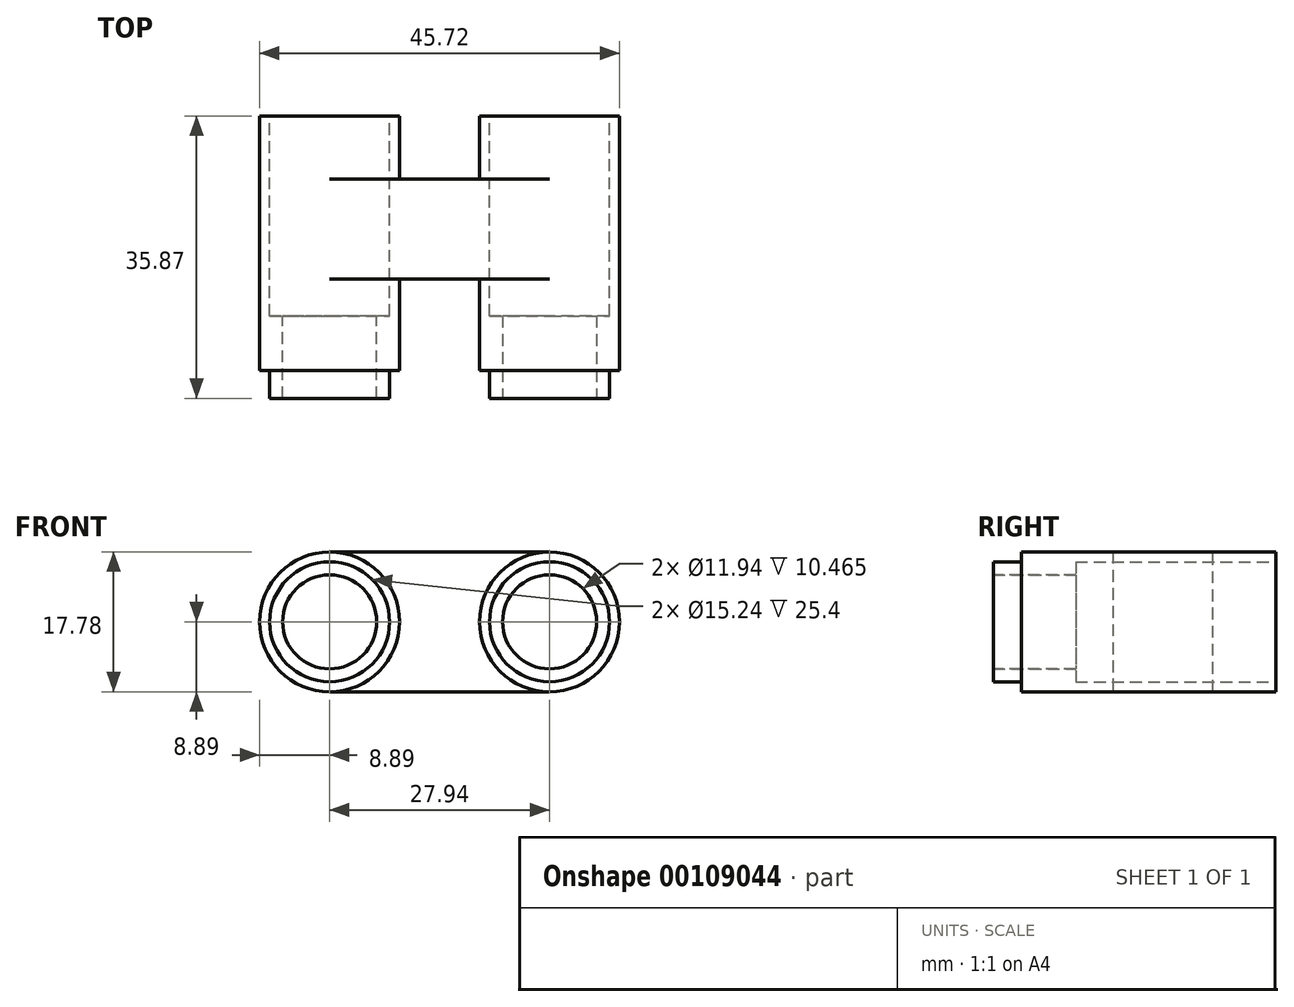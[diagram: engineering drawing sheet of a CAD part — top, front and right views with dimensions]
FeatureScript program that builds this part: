
annotation { "Feature Type Name" : "Feature", "Feature Type Description" : "" }
export const myFeature = defineFeature(function(context is Context, id is Id, definition is map)
    precondition{}
    {
        {
            var Q0;
            Q0=qCreatedBy(makeId("Top.planeOp"),FACE);
            var sketch = newSketch(context, id + "F0", { "sketchPlane" : qUnion([Q0])});
            skLineSegment(sketch, "E0", {"start": v(0, 0) * mm, "end": v(0, 70.4) * mm});
            skArc(sketch, "E1", {"start": v(0, 70.4) * mm, "mid": v(13.97, 84.38) * mm, "end": v(27.94, 70.4) * mm});
            skLineSegment(sketch, "E2", {"start": v(27.94, 70.4) * mm, "end": v(27.94, 0) * mm});
            skLineSegment(sketch, "E3", {"start": v(0, 0) * mm, "end": v(0, -5.08) * mm});
            skLineSegment(sketch, "E4", {"start": v(27.94, 0) * mm, "end": v(27.94, -3.56) * mm});
            skLineSegment(sketch, "E5", {"start": v(-21.52, 32.3) * mm, "end": v(57.2, 32.3) * mm});
            skLineSegment(sketch, "E6", {"start": v(57.2, 32.3) * mm, "end": v(57.2, 105.66) * mm});
            skLineSegment(sketch, "E7", {"start": v(57.2, 105.66) * mm, "end": v(-21.52, 105.66) * mm});
            skLineSegment(sketch, "E8", {"start": v(-21.52, 105.66) * mm, "end": v(-21.52, 32.3) * mm});
            skLineSegment(sketch, "E9", {"start": v(13.97, 70.4) * mm, "end": v(13.97, 32.3) * mm});
            skLineSegment(sketch, "E10", {"start": v(27.94, 24.31) * mm, "end": v(0, 24.31) * mm});
            skLineSegment(sketch, "E11", {"start": v(0, 11.61) * mm, "end": v(27.94, 11.61) * mm});
            skLineSegment(sketch, "E12", {"start": v(17.66, 11.61) * mm, "end": v(17.66, 24.31) * mm});
            skSolve(sketch);
        }
        {
            var Q0;
            Q0=qCreatedBy(makeId("Front.planeOp"),FACE);
            var sketch = newSketch(context, id + "F1", { "sketchPlane" : qUnion([Q0])});
            skCircle(sketch, "E13", {"center": v(0, 0) * mm, "radius": 8.9 * mm});
            skCircle(sketch, "E14", {"center": v(0, 0) * mm, "radius": 5.97 * mm});
            skSolve(sketch);
        }
        {
            var Q0;
            Q0=makeQuery(id+"F1.imprint","IMPRINT",FACE,{"disambiguationData":[TD([[makeQuery(id+"F1.imprint","IMPRINT",EDGE,{"derivedFrom":sQuery(id+"F1.wireOp",EDGE,"E13")}),1.0]])]});
            var Q1;
            Q1=sQuery(id+"F0.wireOp",EDGE,"E0");
            var Q2;
            Q2=sQuery(id+"F0.wireOp",EDGE,"E1");
            var Q3;
            Q3=sQuery(id+"F0.wireOp",EDGE,"E2");
            var Q4;
            Q4=sQuery(id+"F0.wireOp",EDGE,"E4");
            sweep(context, id + "F2", {"profiles" : qUnion([Q0]), "path" : qUnion([Q1, Q2, Q3, Q4])});
        }
        {
            var Q0;
            Q0=makeQuery(id+"F2.opSweep","CAP_FACE",FACE,{"disambiguationData":[OSD([sQuery(id+"F0.wireOp",VERTEX,"E0.start"),sQuery(id+"F1.wireOp",EDGE,"E13"),sQuery(id+"F1.wireOp",EDGE,"E14")])],"isStart":true});
            extrude(context, id + "F3", {"entities" : qUnion([Q0]), "operationType" : NewBodyOperationType.ADD, "depth" : 3.56 * mm});
        }
        {
            var Q0;
            Q0=makeQuery(id+"F3.opExtrude","CAP_FACE",FACE,{"disambiguationData":[OSD([sQuery(id+"F0.wireOp",VERTEX,"E0.start"),sQuery(id+"F1.wireOp",EDGE,"E13"),sQuery(id+"F1.wireOp",EDGE,"E14")])],"isStart":false});
            var sketch = newSketch(context, id + "F4", { "sketchPlane" : qUnion([Q0])});
            skCircle(sketch, "E15", {"center": v(0, 0) * mm, "radius": 7.62 * mm});
            skSolve(sketch);
        }
        {
            var Q0;
            Q0=makeQuery(id+"F2.opSweep","CAP_FACE",FACE,{"disambiguationData":[OSD([sQuery(id+"F0.wireOp",VERTEX,"E4.end"),sQuery(id+"F1.wireOp",EDGE,"E13"),sQuery(id+"F1.wireOp",EDGE,"E14")])],"isStart":false});
            var sketch = newSketch(context, id + "F5", { "sketchPlane" : qUnion([Q0])});
            skCircle(sketch, "E16", {"center": v(27.94, 0) * mm, "radius": 7.62 * mm});
            skSolve(sketch);
        }
        {
            var Q0;
            Q0=makeQuery(id+"F4.imprint","IMPRINT",FACE,{"disambiguationData":[TD([[makeQuery(id+"F4.imprint","IMPRINT",EDGE,{"derivedFrom":sQuery(id+"F4.wireOp",EDGE,"E15")}),-1.0]])]});
            extrude(context, id + "F6", {"entities" : qUnion([Q0]), "operationType" : NewBodyOperationType.REMOVE, "oppositeDirection" : true, "depth" : 3.56 * mm});
        }
        {
            var Q0;
            Q0=makeQuery(id+"F5.imprint","IMPRINT",FACE,{"disambiguationData":[TD([[makeQuery(id+"F5.imprint","IMPRINT",EDGE,{"derivedFrom":sQuery(id+"F5.wireOp",EDGE,"E16")}),-1.0]])]});
            extrude(context, id + "F7", {"entities" : qUnion([Q0]), "operationType" : NewBodyOperationType.REMOVE, "oppositeDirection" : true, "depth" : 3.56 * mm});
        }
        {
            var Q0;
            {var subQ5=sQuery(id+"F0.wireOp",EDGE,"E1");Q0=makeQuery(id+"F0.imprint","IMPRINT",FACE,{"disambiguationData":[TD([[makeQuery(id+"F0.imprint","IMPRINT",EDGE,{"derivedFrom":subQ5}),1.0]])]});}
            var Q1;
            {var subQ5=sQuery(id+"F0.wireOp",EDGE,"E1");Q1=makeQuery(id+"F0.imprint","IMPRINT",FACE,{"disambiguationData":[TD([[makeQuery(id+"F0.imprint","IMPRINT",EDGE,{"derivedFrom":subQ5}),-1.0]])]});}
            extrude(context, id + "F8", {"entities" : qUnion([Q0, Q1]), "operationType" : NewBodyOperationType.REMOVE, "oppositeDirection" : true, "depth" : 25.4 * mm, "hasSecondDirection" : true, "secondDirectionOppositeDirection" : false, "secondDirectionDepth" : 25.4 * mm});
        }
        {
            var Q0;
            Q0=makeQuery(id+"F8.boolean.opBoolean","COPY",FACE,{"disambiguationData":[OD(0.0)],"derivedFrom":makeQuery(id+"F8.opExtrude","SWEPT_FACE",FACE,{"disambiguationData":[OSD([sQuery(id+"F0.wireOp",EDGE,"E5")])]})});
            var sketch = newSketch(context, id + "F9", { "sketchPlane" : qUnion([Q0])});
            skCircle(sketch, "E17", {"center": v(-27.94, 0) * mm, "radius": 7.62 * mm});
            skSolve(sketch);
        }
        {
            var Q0;
            Q0=makeQuery(id+"F8.boolean.opBoolean","COPY",FACE,{"disambiguationData":[OD(1.0)],"derivedFrom":makeQuery(id+"F8.opExtrude","SWEPT_FACE",FACE,{"disambiguationData":[OSD([sQuery(id+"F0.wireOp",EDGE,"E5")])]})});
            var sketch = newSketch(context, id + "F10", { "sketchPlane" : qUnion([Q0])});
            skCircle(sketch, "E18", {"center": v(0, 0) * mm, "radius": 7.62 * mm});
            skSolve(sketch);
        }
        {
            var Q0;
            {var subQ5=sQuery(id+"F0.wireOp",EDGE,"E12");Q0=makeQuery(id+"F0.imprint","IMPRINT",FACE,{"disambiguationData":[TD([[makeQuery(id+"F0.imprint","IMPRINT",EDGE,{"derivedFrom":subQ5}),-1.0]])]});}
            var Q1;
            {var subQ5=sQuery(id+"F0.wireOp",EDGE,"E12");Q1=makeQuery(id+"F0.imprint","IMPRINT",FACE,{"disambiguationData":[TD([[makeQuery(id+"F0.imprint","IMPRINT",EDGE,{"derivedFrom":subQ5}),1.0]])]});}
            extrude(context, id + "F11", {"entities" : qUnion([Q0, Q1]), "operationType" : NewBodyOperationType.ADD, "depth" : 8.9 * mm, "hasSecondDirection" : true, "secondDirectionOppositeDirection" : true, "secondDirectionDepth" : 8.9 * mm});
        }
        {
            var Q0;
            Q0=makeQuery(id+"F9.imprint","IMPRINT",FACE,{"disambiguationData":[TD([[makeQuery(id+"F9.imprint","IMPRINT",EDGE,{"derivedFrom":sQuery(id+"F9.wireOp",EDGE,"E17")}),1.0]])]});
            var Q1;
            Q1=makeQuery(id+"F10.imprint","IMPRINT",FACE,{"disambiguationData":[TD([[makeQuery(id+"F10.imprint","IMPRINT",EDGE,{"derivedFrom":sQuery(id+"F10.wireOp",EDGE,"E18")}),1.0]])]});
            var Q2;
            Q2=makeQuery(id+"F9.imprint","IMPRINT",FACE,{"disambiguationData":[TD([[makeQuery(id+"F9.imprint","IMPRINT",EDGE,{"derivedFrom":makeQuery(id+"F8.boolean.opBoolean","INTERSECT",EDGE,{"derivedFrom":[makeQuery(id+"F2.opSweep","SWEPT_FACE",FACE,{"disambiguationData":[OSD([sQuery(id+"F0.wireOp",EDGE,"E4"),sQuery(id+"F1.wireOp",EDGE,"E14")])]}),makeQuery(id+"F8.opExtrude","SWEPT_FACE",FACE,{"disambiguationData":[OSD([sQuery(id+"F0.wireOp",EDGE,"E5")])]})]})}),-1.0]])]});
            var Q3;
            {var subQ0=sQuery(id+"F1.wireOp",EDGE,"E14");Q3=makeQuery(id+"F10.imprint","IMPRINT",FACE,{"disambiguationData":[TD([[makeQuery(id+"F10.imprint","IMPRINT",EDGE,{"derivedFrom":makeQuery(id+"F8.boolean.opBoolean","INTERSECT",EDGE,{"derivedFrom":[makeQuery(id+"F3.boolean.opBoolean","MERGE",FACE,{"derivedFrom":[makeQuery(id+"F2.opSweep","SWEPT_FACE",FACE,{"disambiguationData":[OSD([sQuery(id+"F0.wireOp",EDGE,"E0"),subQ0])]}),makeQuery(id+"F3.opExtrude","SWEPT_FACE",FACE,{"disambiguationData":[OSD([sQuery(id+"F0.wireOp",VERTEX,"E0.start"),subQ0])]})]}),makeQuery(id+"F8.opExtrude","SWEPT_FACE",FACE,{"disambiguationData":[OSD([sQuery(id+"F0.wireOp",EDGE,"E5")])]})]})}),-1.0]])]});}
            extrude(context, id + "F12", {"entities" : qUnion([Q0, Q1, Q2, Q3]), "operationType" : NewBodyOperationType.REMOVE, "oppositeDirection" : true, "depth" : 25.4 * mm});
        }
    });
